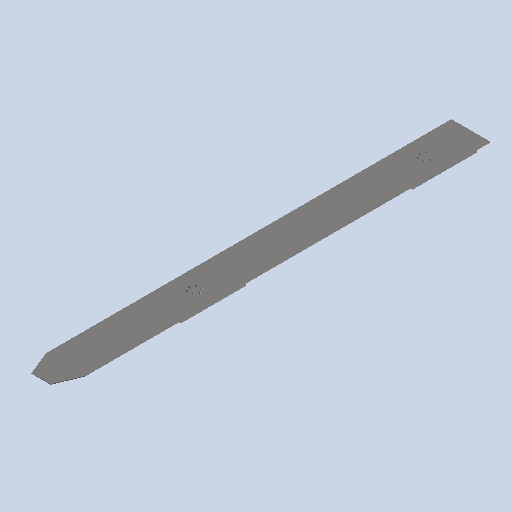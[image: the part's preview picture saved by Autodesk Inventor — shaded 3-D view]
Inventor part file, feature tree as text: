
AUTODESK INVENTOR PART (.ipt)
format: ipt  version: 2022.1 (Build 261234000, 234)  size: 172,032 bytes
history: native  units: mm
features: reference x37, other x10, sketch x3, sheet_metal_op x2, hole x1, projected_geometry x1
ambient origin geometry x8: Origin, YZ Plane, XZ Plane, XY Plane, X Axis, Y Axis, Z Axis, Center Point
bodies: Solid1 (feature_tree), Solid2 (feature_tree)
feature tree (54):
  sheet_metal_op  "Face1"
  hole  "Hole1"  [1 undecoded]
  sheet_metal_op  "Face2"
  sketch  "Sketch1"  dims[d0=8.0mm]
  reference  "Reference1"
  reference  "Reference2"
  reference  "Reference3"
  reference  "Reference4"
  reference  "Reference5"
  reference  "Reference6"
  other  "Plate1"
  reference  "Reference7"
  reference  "Reference8"
  sketch  "Sketch2"  dims[d4=4.5mm d5=26.0mm d6=8.0mm d7=4.6mm d8=90.0deg d9=8.0mm d10=20.594885mm]
  reference  "Reference9"
  reference  "Reference10"
  reference  "Reference11"
  reference  "Reference12"
  reference  "Reference13"
  reference  "Reference14"
  reference  "Reference15"
  reference  "Reference16"
  reference  "Reference17"
  reference  "Reference18"
  reference  "Reference19"
  projected_geometry  "Projected Loop1"
  reference  "Reference20"
  reference  "Reference21"
  reference  "Reference22"
  reference  "Reference23"
  reference  "Reference24"
  reference  "Reference25"
  reference  "Reference26"
  reference  "Reference27"
  reference  "Reference28"
  sketch  "Sketch3"  dims[d11=30.0mm d12=200.0mm d13=200.0mm d14=2.0mm]
  reference  "Reference29"
  reference  "Reference30"
  reference  "Reference31"
  reference  "Reference32"
  reference  "Reference33"
  reference  "Reference34"
  reference  "Reference35"
  reference  "Reference36"
  reference  "Reference37"
  other  "Plate2"
  other  "HorquillaSuperior.iam"
  other  "HorquillaSuperior:1"
  other  "RobotPallet.iam"
  other  "SistemaElevacion2:2"
  other  "BridaTornillo2:1"
  other  "SistemaElevacion2:1"
  other  "Frame_HorqSup:1"
  other  "ISO 657-1 L60x60x8 - 2815.41:1"
note: 1 required parameter value undecoded (feature->parameter linkage not recoverable at this tier; creation-order binding heuristic only, values carry confidence <= 0.55)
